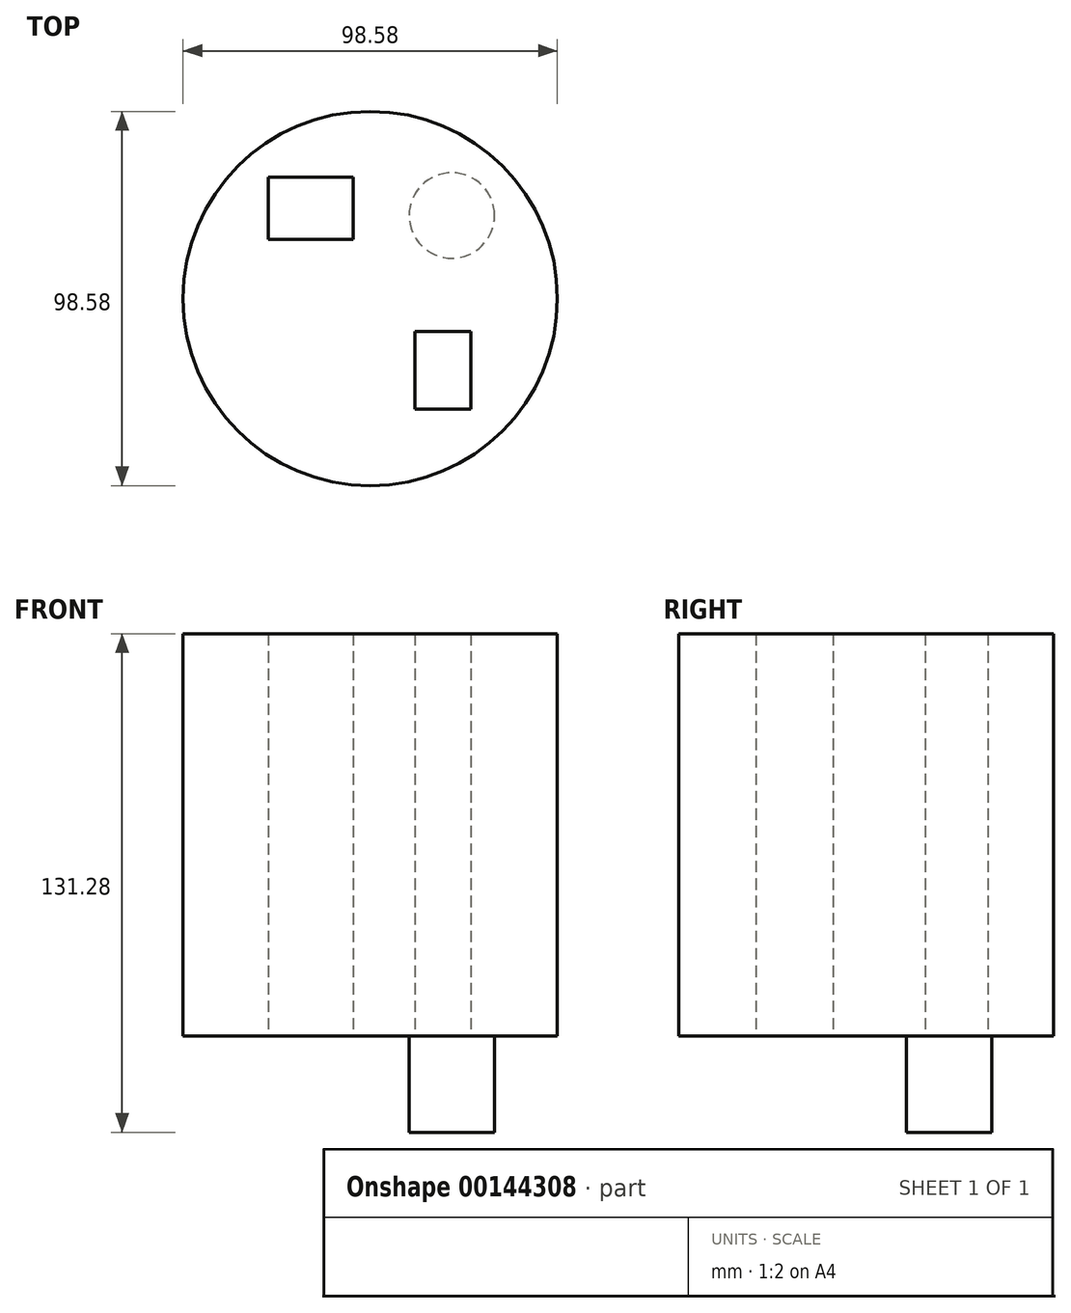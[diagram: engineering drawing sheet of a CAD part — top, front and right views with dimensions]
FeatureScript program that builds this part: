
annotation { "Feature Type Name" : "Feature", "Feature Type Description" : "" }
export const myFeature = defineFeature(function(context is Context, id is Id, definition is map)
    precondition{}
    {
        {
            var Q0;
            Q0=qCreatedBy(makeId("Top.planeOp"),FACE);
            var sketch = newSketch(context, id + "F0", { "sketchPlane" : qUnion([Q0])});
            skCircle(sketch, "E0", {"center": v(0, 0) * mm, "radius": 49.3 * mm});
            skLineSegment(sketch, "E1.bottom", {"start": v(-26.83, 15.57) * mm, "end": v(-4.5, 15.57) * mm});
            skLineSegment(sketch, "E1.top", {"start": v(-26.83, 32.02) * mm, "end": v(-4.5, 32.02) * mm});
            skLineSegment(sketch, "E1.left", {"start": v(-26.83, 15.57) * mm, "end": v(-26.83, 32.02) * mm});
            skLineSegment(sketch, "E1.right", {"start": v(-4.5, 15.57) * mm, "end": v(-4.5, 32.02) * mm});
            skLineSegment(sketch, "E2.bottom", {"start": v(11.75, -29.09) * mm, "end": v(26.44, -29.09) * mm});
            skLineSegment(sketch, "E2.top", {"start": v(11.75, -8.72) * mm, "end": v(26.44, -8.72) * mm});
            skLineSegment(sketch, "E2.left", {"start": v(11.75, -29.09) * mm, "end": v(11.75, -8.72) * mm});
            skLineSegment(sketch, "E2.right", {"start": v(26.44, -29.09) * mm, "end": v(26.44, -8.72) * mm});
            skSolve(sketch);
        }
        {
            var Q0;
            Q0 = qSketchRegion(id + "F0", true);
            extrude(context, id + "F1", {"entities" : qUnion([Q0]), "depth" : 105.88 * mm});
        }
        {
            var Q0;
            Q0=makeQuery(id+"F1.opExtrude","CAP_FACE",FACE,{"disambiguationData":[OSD([sQuery(id+"F0.wireOp",EDGE,"E0"),sQuery(id+"F0.wireOp",EDGE,"E1.bottom"),sQuery(id+"F0.wireOp",EDGE,"E1.top"),sQuery(id+"F0.wireOp",EDGE,"E1.left"),sQuery(id+"F0.wireOp",EDGE,"E1.right"),sQuery(id+"F0.wireOp",EDGE,"E2.bottom"),sQuery(id+"F0.wireOp",EDGE,"E2.top"),sQuery(id+"F0.wireOp",EDGE,"E2.left"),sQuery(id+"F0.wireOp",EDGE,"E2.right")])],"isStart":true});
            var sketch = newSketch(context, id + "F2", { "sketchPlane" : qUnion([Q0])});
            skCircle(sketch, "E3", {"center": v(21.49, -21.87) * mm, "radius": 11.25 * mm});
            skSolve(sketch);
        }
        {
            var Q0;
            Q0 = qSketchRegion(id + "F2", true);
            extrude(context, id + "F3", {"entities" : qUnion([Q0]), "operationType" : NewBodyOperationType.ADD, "depth" : 25.4 * mm});
        }
    });
